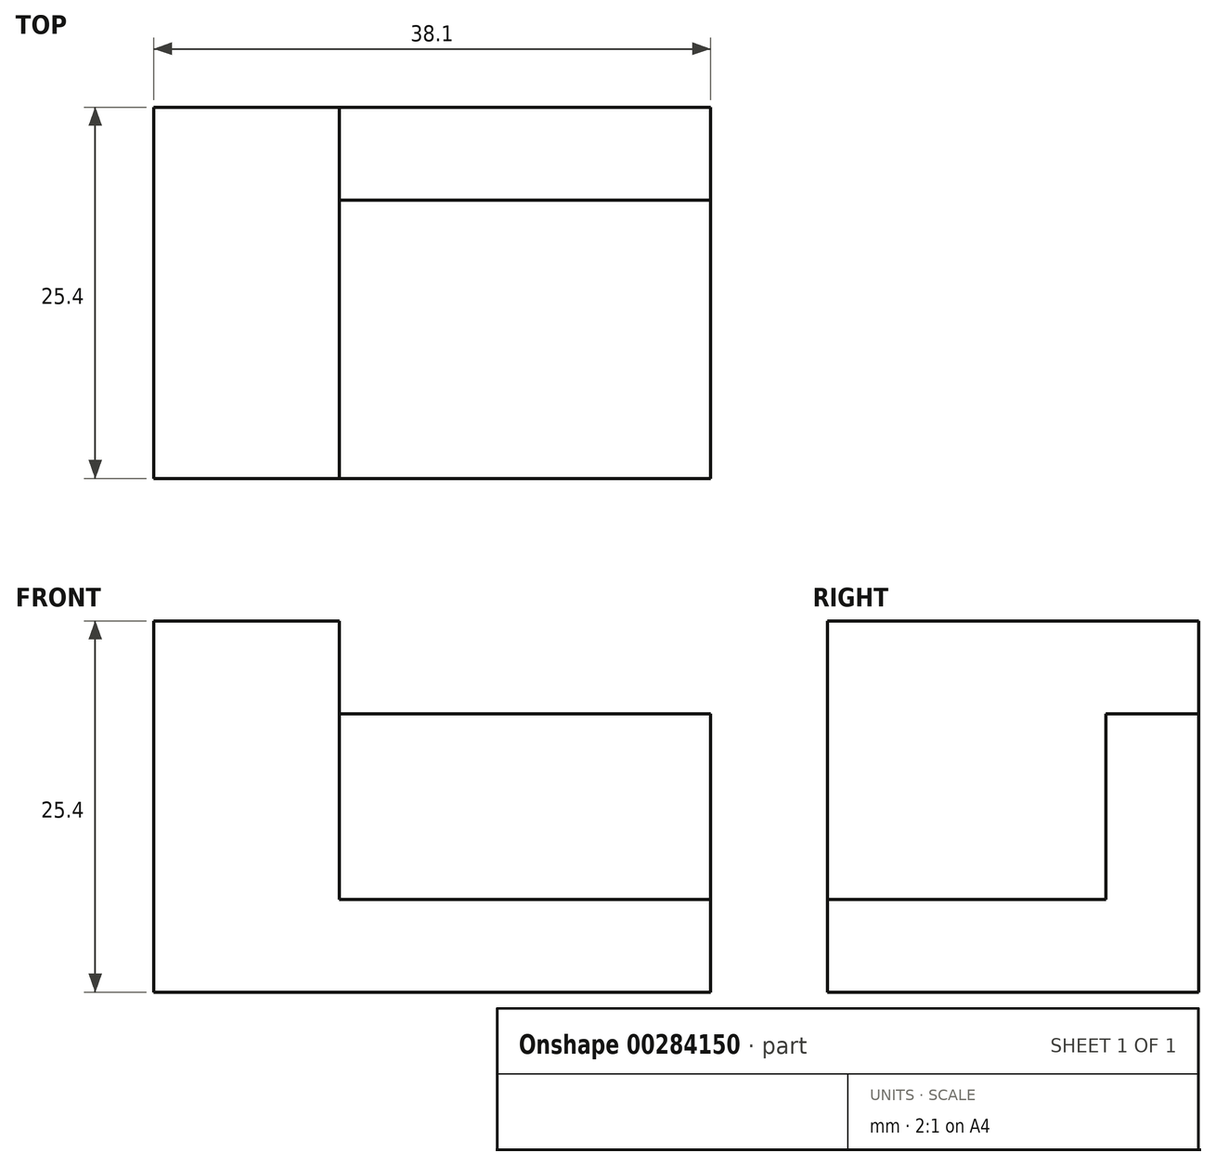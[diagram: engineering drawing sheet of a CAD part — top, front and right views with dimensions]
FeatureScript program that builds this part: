
annotation { "Feature Type Name" : "Feature", "Feature Type Description" : "" }
export const myFeature = defineFeature(function(context is Context, id is Id, definition is map)
    precondition{}
    {
        {
            var Q0;
            Q0=qCreatedBy(makeId("Top.planeOp"),FACE);
            var sketch = newSketch(context, id + "F0", { "sketchPlane" : qUnion([Q0])});
            skLineSegment(sketch, "E0.bottom", {"start": v(0, 0) * mm, "end": v(38.1, 0) * mm});
            skLineSegment(sketch, "E0.top", {"start": v(0, -25.4) * mm, "end": v(38.1, -25.4) * mm});
            skLineSegment(sketch, "E0.left", {"start": v(0, 0) * mm, "end": v(0, -25.4) * mm});
            skLineSegment(sketch, "E0.right", {"start": v(38.1, 0) * mm, "end": v(38.1, -25.4) * mm});
            skSolve(sketch);
        }
        {
            var Q0;
            Q0=makeQuery(id+"F0.imprint","IMPRINT",FACE,{"disambiguationData":[TD([[makeQuery(id+"F0.imprint","IMPRINT",EDGE,{"derivedFrom":sQuery(id+"F0.wireOp",EDGE,"E0.bottom")}),-1.0]])]});
            extrude(context, id + "F1", {"entities" : qUnion([Q0]), "depth" : 25.4 * mm});
        }
        {
            var Q0;
            Q0=makeQuery(id+"F1.opExtrude","SWEPT_FACE",FACE,{"disambiguationData":[OSD([sQuery(id+"F0.wireOp",EDGE,"E0.top")])]});
            var sketch = newSketch(context, id + "F2", { "sketchPlane" : qUnion([Q0])});
            skLineSegment(sketch, "E1.bottom", {"start": v(12.7, 25.4) * mm, "end": v(38.1, 25.4) * mm});
            skLineSegment(sketch, "E1.top", {"start": v(12.7, 6.35) * mm, "end": v(38.1, 6.35) * mm});
            skLineSegment(sketch, "E1.left", {"start": v(12.7, 25.4) * mm, "end": v(12.7, 6.35) * mm});
            skLineSegment(sketch, "E1.right", {"start": v(38.1, 25.4) * mm, "end": v(38.1, 6.35) * mm});
            skSolve(sketch);
        }
        {
            var Q0;
            Q0 = qSketchRegion(id + "F2", true);
            extrude(context, id + "F3", {"entities" : qUnion([Q0]), "operationType" : NewBodyOperationType.REMOVE, "oppositeDirection" : true, "depth" : 19.05 * mm});
        }
        {
            var Q0;
            Q0=makeQuery(id+"F1.opExtrude","CAP_FACE",FACE,{"disambiguationData":[OSD([sQuery(id+"F0.wireOp",EDGE,"E0.bottom"),sQuery(id+"F0.wireOp",EDGE,"E0.top"),sQuery(id+"F0.wireOp",EDGE,"E0.left"),sQuery(id+"F0.wireOp",EDGE,"E0.right")])],"isStart":false});
            var sketch = newSketch(context, id + "F4", { "sketchPlane" : qUnion([Q0])});
            skLineSegment(sketch, "E2.bottom", {"start": v(38.1, -6.35) * mm, "end": v(12.7, -6.35) * mm});
            skLineSegment(sketch, "E2.top", {"start": v(38.1, 0) * mm, "end": v(12.7, 0) * mm});
            skLineSegment(sketch, "E2.left", {"start": v(38.1, -6.35) * mm, "end": v(38.1, 0) * mm});
            skLineSegment(sketch, "E2.right", {"start": v(12.7, -6.35) * mm, "end": v(12.7, 0) * mm});
            skSolve(sketch);
        }
        {
            var Q0;
            Q0 = qSketchRegion(id + "F4", true);
            extrude(context, id + "F5", {"entities" : qUnion([Q0]), "operationType" : NewBodyOperationType.REMOVE, "oppositeDirection" : true, "depth" : 6.35 * mm});
        }
    });
